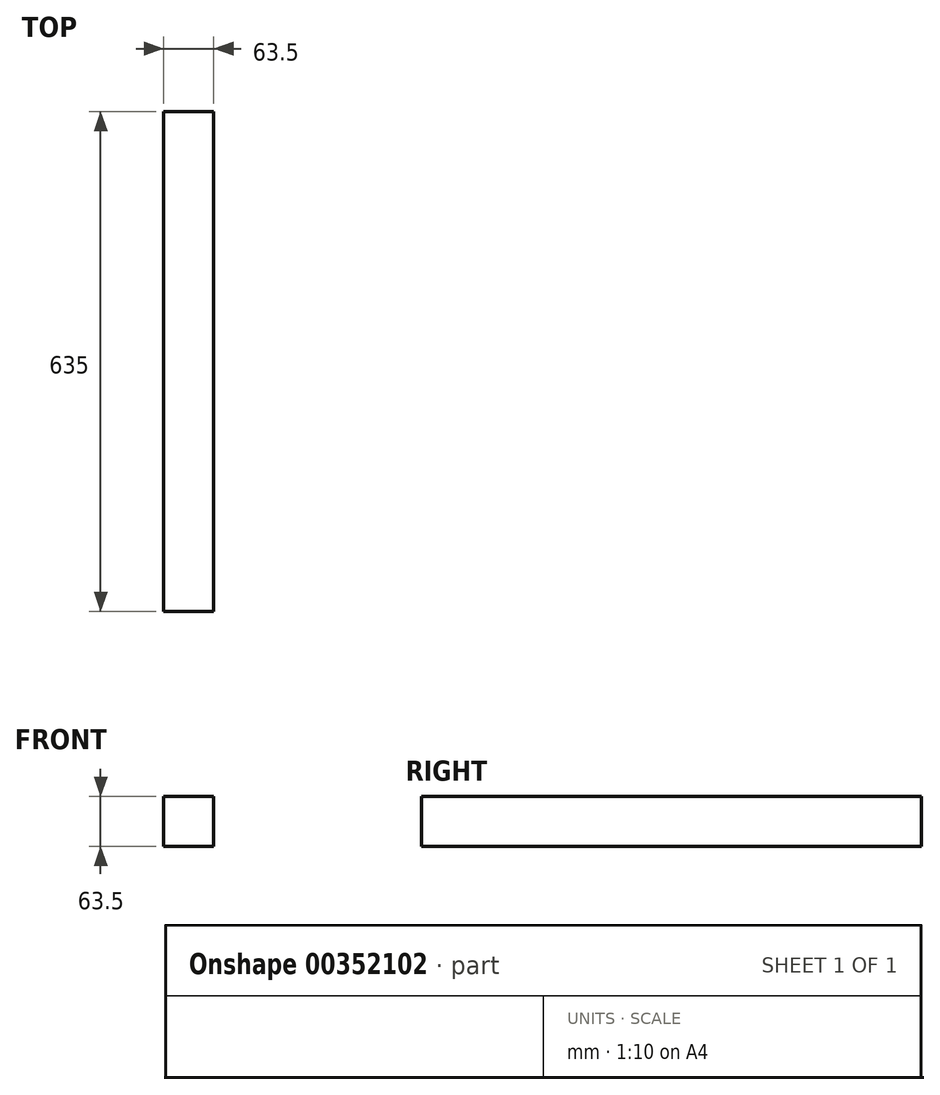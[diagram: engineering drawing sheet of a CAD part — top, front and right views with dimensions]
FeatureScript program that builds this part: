
annotation { "Feature Type Name" : "Feature", "Feature Type Description" : "" }
export const myFeature = defineFeature(function(context is Context, id is Id, definition is map)
    precondition{}
    {
        {
            var Q0;
            Q0=qCreatedBy(makeId("Front.planeOp"),FACE);
            var sketch = newSketch(context, id + "F0", { "sketchPlane" : qUnion([Q0])});
            skLineSegment(sketch, "E0.bottom", {"start": v(31.75, -31.75) * mm, "end": v(-31.75, -31.75) * mm});
            skLineSegment(sketch, "E0.top", {"start": v(31.75, 31.75) * mm, "end": v(-31.75, 31.75) * mm});
            skLineSegment(sketch, "E0.left", {"start": v(31.75, -31.75) * mm, "end": v(31.75, 31.75) * mm});
            skLineSegment(sketch, "E0.right", {"start": v(-31.75, -31.75) * mm, "end": v(-31.75, 31.75) * mm});
            skPoint(sketch, "E0.middle", {"position": v(0, 0) * mm});
            skSolve(sketch);
        }
        {
            var Q0;
            Q0 = qSketchRegion(id + "F0", true);
            extrude(context, id + "F1", {"entities" : qUnion([Q0]), "depth" : 635 * mm});
        }
    });
